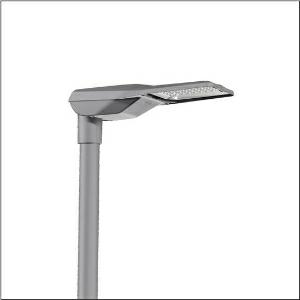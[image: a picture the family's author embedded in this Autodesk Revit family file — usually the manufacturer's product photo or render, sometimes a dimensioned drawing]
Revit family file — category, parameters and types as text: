
# Revit family: streetlight_sl_21_iq_mini___pl52_5xe2h31g08gb_d0f1
name_source: partatom
category: Lighting Fixtures
units: mm (PartAtom-declared; Revit-internal decimal feet)

## family parameters
Cut with Voids When Loaded = No
Host = Face
Light Source = No
Part Type = Normal
Room Calculation Point = No
Round Connector Dimension = Use Diameter
Shared = No

## types (1)
- --- (1 x LED, 5580 lm, 37.1 W, 3000K)
    Apparent Load = 37 VA
    CIE Flux Codes = 27 59 98 100 100
    Color Rendering = 70
    Color Temperature = 3000K
    Default Elevation = 1800 mm
    Description = Streetlight SL 21 mini, mast luminaire, primary light control with lens, of PMMA, primary optical cover: cover, of toughened safety glass, transparent, light distribution: PL52, light emission: direct distribution, primary light characteristic: asymmetric, installation type: post-top, side-entry, LED, High Power LED, rated luminous flux: 5.580lm, luminous efficacy: 150lm/W, light colour: 730, colour temperature: 3000K, control gear: ECG iQ, control: Street-Remote, Auto-Match, Temp-Guard, Lumen-Switch, Night-Set, Smart-Wire, Light-Fading, Desk-Remote (wireless, voltage-free reading and setting of iQ features in the workshop via application-optimized NFC function/RFID function), optimised constant luminous flux control (CLO 2.0), mains connection: 220..240V, AC, 50/60Hz, start of lifetime: 37W, end of lifetime: 39W, reduction: 18W, luminaire housing, of diecast aluminium, powder-coated, Siteco® metallic grey (DB 702S), corrosivity category C5 according to DIN EN ISO 12944, length: 628mm, width: 235mm, height: 110mm, spigot size: 60/76mm (post-top) and 42/60/76mm (side-entry), mast flange for spigot size: 42mm: 5XC10008XM4, 60mm: 5XC10008XM2, 76/60mm: 5XC10108XM1, protection rating (complete): IP66, insulation class (complete): insulation class II (safety insulation), certification: CE, ENEC, VDE, impact resistance: IK09, permissible operating ambient temperature for outdoor applications: -40..+50°C, standard-compliant lighting for roads and squares, packaging unit: 1 piece

Light Distribution: PL52
    Height = 110 mm
    Lamp = 1 x LED
    Lamp Light Flux = 5580 lm
    Lamp Power = 37.1 W
    Lamp count = 1
    Length = 625 mm
    Luminous efficacy = 150 lm/W
    Manufacturer = Siteco
    ModVariant = No
    Model = 5XE2H31G08GB
    Number of Poles = 1
    OnlyDefault = Yes
    Power Factor = 1
    Product Name = Streetlight SL 21 iQ mini | PL52
    Product group = mast luminaire | pylon top
    ProductGroupID = 6100
    Protection Class = Protection class II
    Protection Degree = IP 66
    RLX_Detail_Level = 1
    RlxData = <blob elided: 103413 chars, md5=a7555c3a>
    Socket = socket
    Standby Power = 0 W
    System Light Flux = 5580 lm
    System Power = 37 W
    Type Comments = factory setting: luminous flux: 100 % | dim-lin: 254 | 385 mA
    Type Image = l_1003519.jpg
    URL = http://relux.com
    VarID = @adj_109531
    Voltage = 0 V
    Weight = 0.00 kg
    Width = 234 mm

## geometry (parser evidence)
native form markers: Blend x4, Sweep x10
no freeform markers — native parametric forms only
